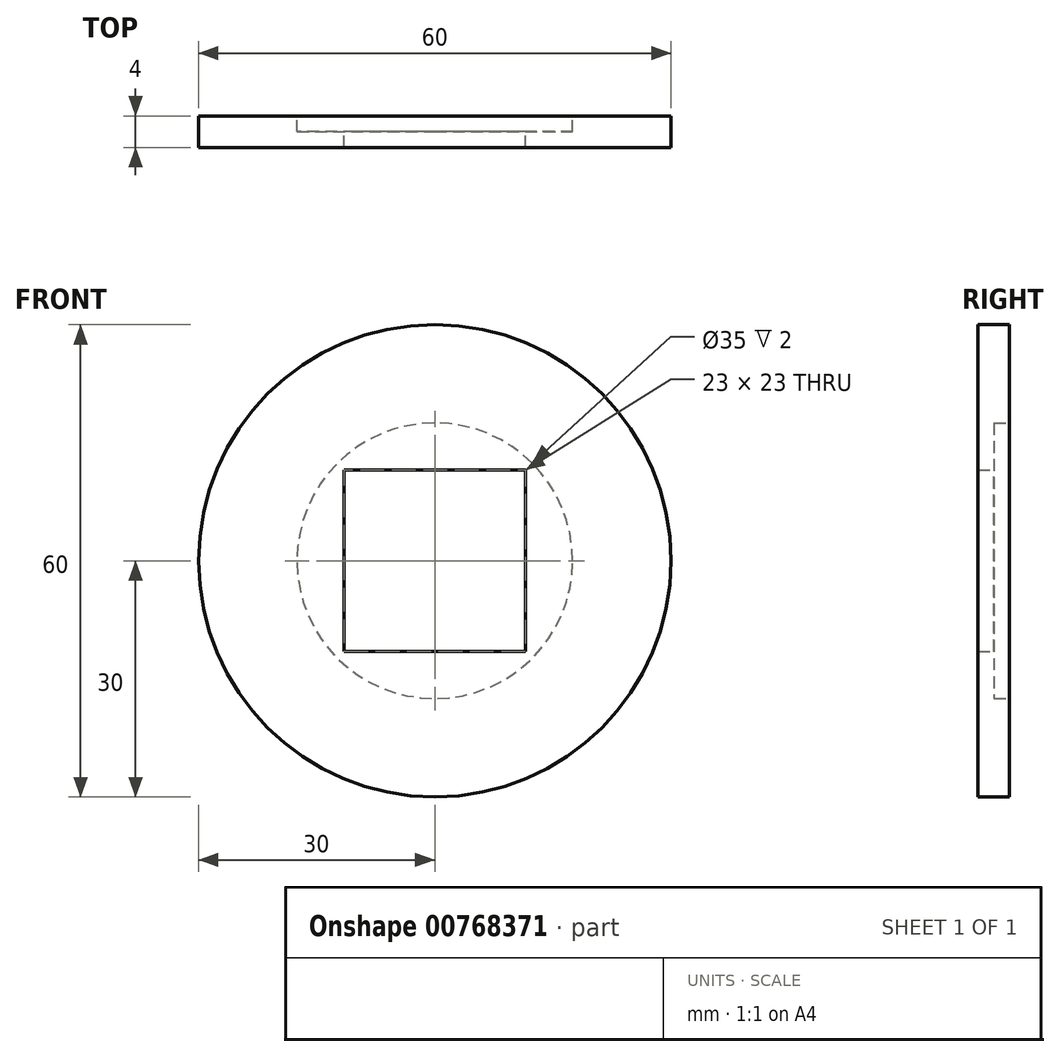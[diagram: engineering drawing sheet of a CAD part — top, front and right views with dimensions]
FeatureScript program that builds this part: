
annotation { "Feature Type Name" : "Feature", "Feature Type Description" : "" }
export const myFeature = defineFeature(function(context is Context, id is Id, definition is map)
    precondition{}
    {
        {
            var Q0;
            Q0=qCreatedBy(makeId("Front.planeOp"),FACE);
            var sketch = newSketch(context, id + "F0", { "sketchPlane" : qUnion([Q0])});
            skCircle(sketch, "E0", {"center": v(0, 0) * mm, "radius": 30 * mm});
            skLineSegment(sketch, "E1.bottom", {"start": v(-11.5, 11.5) * mm, "end": v(11.5, 11.5) * mm});
            skLineSegment(sketch, "E1.top", {"start": v(-11.5, -11.5) * mm, "end": v(11.5, -11.5) * mm});
            skLineSegment(sketch, "E1.left", {"start": v(-11.5, 11.5) * mm, "end": v(-11.5, -11.5) * mm});
            skLineSegment(sketch, "E1.right", {"start": v(11.5, 11.5) * mm, "end": v(11.5, -11.5) * mm});
            skSolve(sketch);
        }
        {
            var Q0;
            Q0=makeQuery(id+"F0.imprint","IMPRINT",FACE,{"disambiguationData":[TD([[makeQuery(id+"F0.imprint","IMPRINT",EDGE,{"derivedFrom":sQuery(id+"F0.wireOp",EDGE,"E0")}),1.0]])]});
            extrude(context, id + "F1", {"entities" : qUnion([Q0]), "depth" : 4 * mm, "offsetDistance" : 25 * mm});
        }
        {
            var Q0;
            Q0=makeQuery(id+"F1.opExtrude","CAP_FACE",FACE,{"disambiguationData":[OSD([sQuery(id+"F0.wireOp",EDGE,"E0"),sQuery(id+"F0.wireOp",EDGE,"E1.bottom"),sQuery(id+"F0.wireOp",EDGE,"E1.top"),sQuery(id+"F0.wireOp",EDGE,"E1.left"),sQuery(id+"F0.wireOp",EDGE,"E1.right")])],"isStart":true});
            var sketch = newSketch(context, id + "F2", { "sketchPlane" : qUnion([Q0])});
            skCircle(sketch, "E2", {"center": v(0, 0) * mm, "radius": 17.5 * mm});
            skSolve(sketch);
        }
        {
            var Q0;
            Q0=makeQuery(id+"F2.imprint","IMPRINT",FACE,{"disambiguationData":[TD([[makeQuery(id+"F2.imprint","IMPRINT",EDGE,{"derivedFrom":sQuery(id+"F2.wireOp",EDGE,"E2")}),1.0]])]});
            var Q1;
            Q1=makeQuery(id+"F2.imprint","IMPRINT",FACE,{"disambiguationData":[TD([[makeQuery(id+"F2.imprint","IMPRINT",EDGE,{"derivedFrom":makeQuery(id+"F1.opExtrude","CAP_EDGE",EDGE,{"disambiguationData":[OSD([sQuery(id+"F0.wireOp",EDGE,"E1.bottom")])],"isStart":true})}),1.0]])]});
            extrude(context, id + "F3", {"entities" : qUnion([Q0, Q1]), "operationType" : NewBodyOperationType.REMOVE, "oppositeDirection" : true, "depth" : 2 * mm, "offsetDistance" : 25 * mm});
        }
    });
